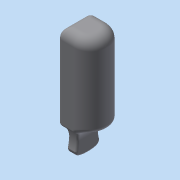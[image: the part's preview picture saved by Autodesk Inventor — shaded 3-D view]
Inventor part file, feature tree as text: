
AUTODESK INVENTOR PART (.ipt)
format: ipt  version: 2015 SP1 (Build 190203100, 203)  size: 652,800 bytes
history: native  units: in
note: dims shown in document units (in); Inventor stores cm internally (conversion verified against a paired STEP export)
features: fillet x12, extrude x4, sketch x4, chamfer x2, projected_geometry x1
ambient origin geometry x8: Origin, YZ Plane, XZ Plane, XY Plane, X Axis, Y Axis, Z Axis, Center Point
bodies: Solid1 (feature_tree)
feature tree (23):
  extrude  "Extrusion1"  Depth=1.378in
  fillet  "Fillet1"  Radius=4.5276in
  fillet  "Fillet2"  Radius=0.1969in
  extrude  "Extrusion2"  Depth=0.9843in
  chamfer  "Chamfer1"  Distance=4.5276in
  fillet  "Fillet3"  Radius=0.9843in
  fillet  "Fillet4"  Radius=0.1969in
  extrude  "Extrusion3"  Depth=1.378in
  chamfer  "Chamfer2"  Distance=1.378in
  fillet  "Fillet5"  Radius=4.5276in
  fillet  "Fillet6"  Radius=0.1181in
  fillet  "Fillet7"  Radius=0.1969in
  extrude  "Extrusion4"  Depth=0.1969in
  fillet  "Fillet8"  Radius=0.3937in
  fillet  "Fillet9"  Radius=0.1969in
  fillet  "Fillet10"  Radius=0.9843in
  fillet  "Fillet11"  Radius=0.7874in
  fillet  "Fillet12"  Radius=1.1811in
  sketch  "Sketch1"  dims[d0=1.378in d1=1.378in d2=4.5276in d3=0.0in d4=0.1969in]
  sketch  "Sketch2"  dims[d5=0.6693in d6=0.9843in]
  sketch  "Sketch3"  dims[d7=0.9843in d8=4.5276in d9=0.0in]
  projected_geometry  "Projected Loop1"
  sketch  "Sketch4"  dims[d10=0.0984in d11=0.125in d12=45.0deg d13=0.9843in d14=0.1969in d15=1.378in d16=1.378in d17=4.5276in d18=0.0in d19=0.1181in d20=0.125in d21=45.0deg d22=0.1969in d23=0.1969in d24=0.3937in d25=0.1969in d26=0.9843in d27=0.7874in d28=1.1811in d29=4.5276in d30=0.0in d31=0.5906in d32=0.1969in d33=0.3937in d34=0.0787in d35=0.0787in]
